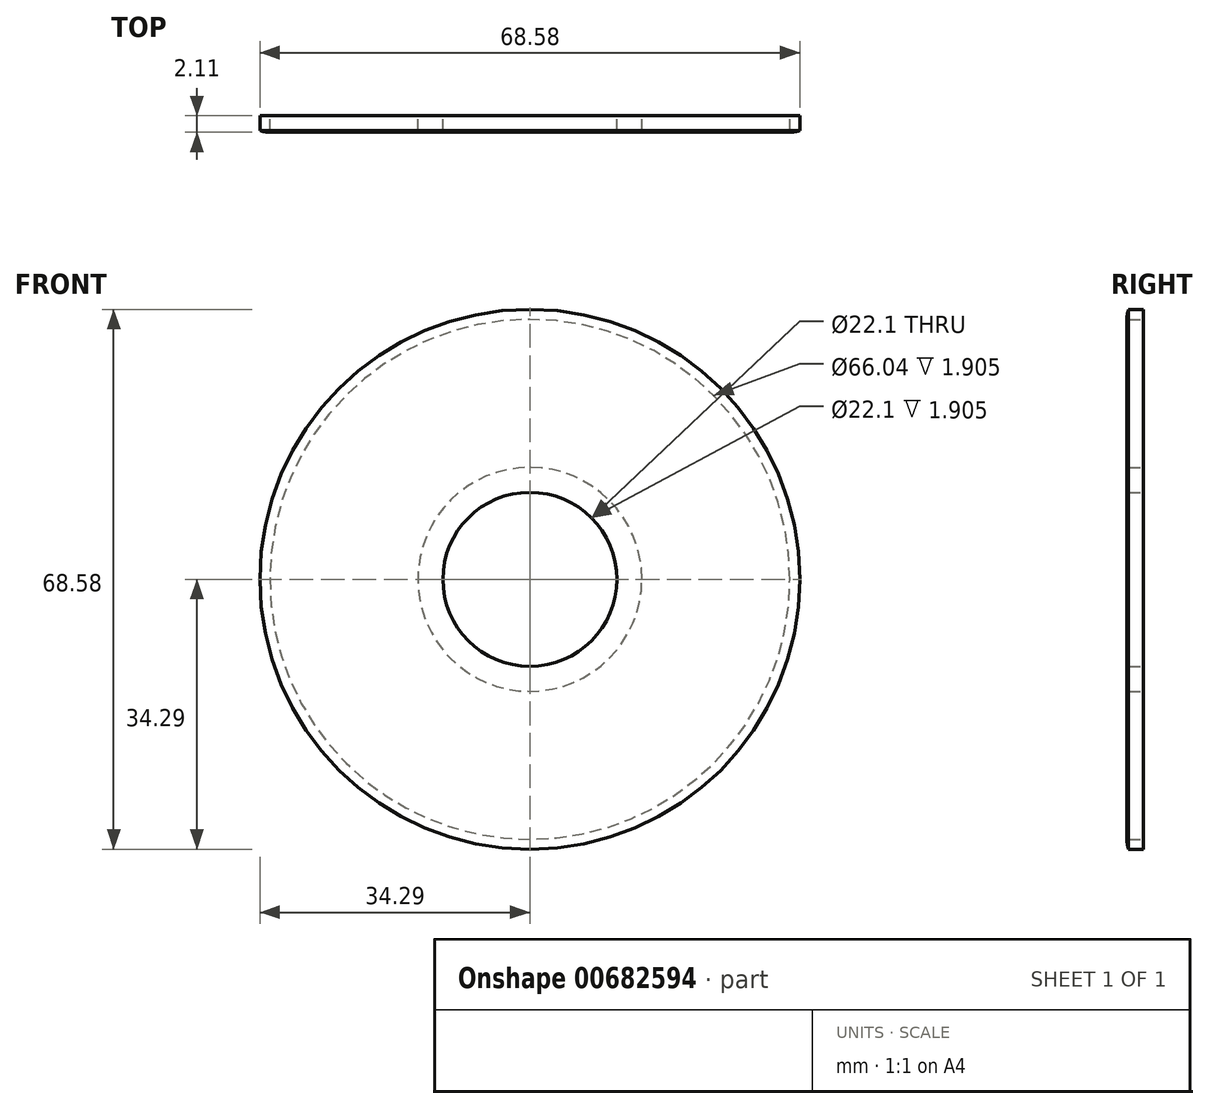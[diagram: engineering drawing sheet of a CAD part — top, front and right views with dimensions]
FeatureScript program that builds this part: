
annotation { "Feature Type Name" : "Feature", "Feature Type Description" : "" }
export const myFeature = defineFeature(function(context is Context, id is Id, definition is map)
    precondition{}
    {
        {
            var Q0;
            Q0=qCreatedBy(makeId("Front.planeOp"),FACE);
            var sketch = newSketch(context, id + "F0", { "sketchPlane" : qUnion([Q0])});
            skCircle(sketch, "E0", {"center": v(0, 0) * mm, "radius": 33.02 * mm});
            skCircle(sketch, "E1", {"center": v(0, 0) * mm, "radius": 34.3 * mm});
            skCircle(sketch, "E2", {"center": v(0, 0) * mm, "radius": 14.22 * mm});
            skCircle(sketch, "E3", {"center": v(0, 0) * mm, "radius": 11.05 * mm});
            skSolve(sketch);
        }
        {
            var Q0;
            Q0 = qSketchRegion(id + "F0", true);
            var Q1;
            Q1=makeQuery(id+"F0.imprint","IMPRINT",FACE,{"disambiguationData":[TD([[makeQuery(id+"F0.imprint","IMPRINT",EDGE,{"derivedFrom":sQuery(id+"F0.wireOp",EDGE,"E2")}),1.0]])]});
            extrude(context, id + "F1", {"entities" : qUnion([Q0, Q1]), "depth" : 1.9 * mm, "offsetDistance" : 25.4 * mm});
        }
        {
            var Q0;
            Q0=makeQuery(id+"F1.opExtrude","CAP_FACE",FACE,{"disambiguationData":[OSD([sQuery(id+"F0.wireOp",EDGE,"E2"),sQuery(id+"F0.wireOp",EDGE,"E3")])],"isStart":false});
            var sketch = newSketch(context, id + "F2", { "sketchPlane" : qUnion([Q0])});
            skCircle(sketch, "E4.0", {"center": v(0, 0) * mm, "radius": 11.05 * mm});
            skCircle(sketch, "E5.0", {"center": v(0, 0) * mm, "radius": 34.3 * mm});
            skSolve(sketch);
        }
        {
            var Q0;
            Q0 = qSketchRegion(id + "F2", true);
            extrude(context, id + "F3", {"entities" : qUnion([Q0]), "depth" : (.28 - (.15 / 2)) * mm, "offsetDistance" : 25.4 * mm});
        }
        {
            var Q0;
            Q0=makeQuery(id+"F3.opExtrude","CAP_EDGE",EDGE,{"disambiguationData":[OSD([sQuery(id+"F2.wireOp",EDGE,"E5.0")])],"isStart":false});
            var Q1;
            Q1=makeQuery(id+"F1.opExtrude","CAP_EDGE",EDGE,{"disambiguationData":[OSD([sQuery(id+"F0.wireOp",EDGE,"E2")])],"isStart":false});
            fillet(context, id + "F4", {"entities" : qUnion([Q0, Q1]), "radius" : 5.08 * mm, "tangentPropagation" : true, "allowEdgeOverflow" : false});
        }
    });
